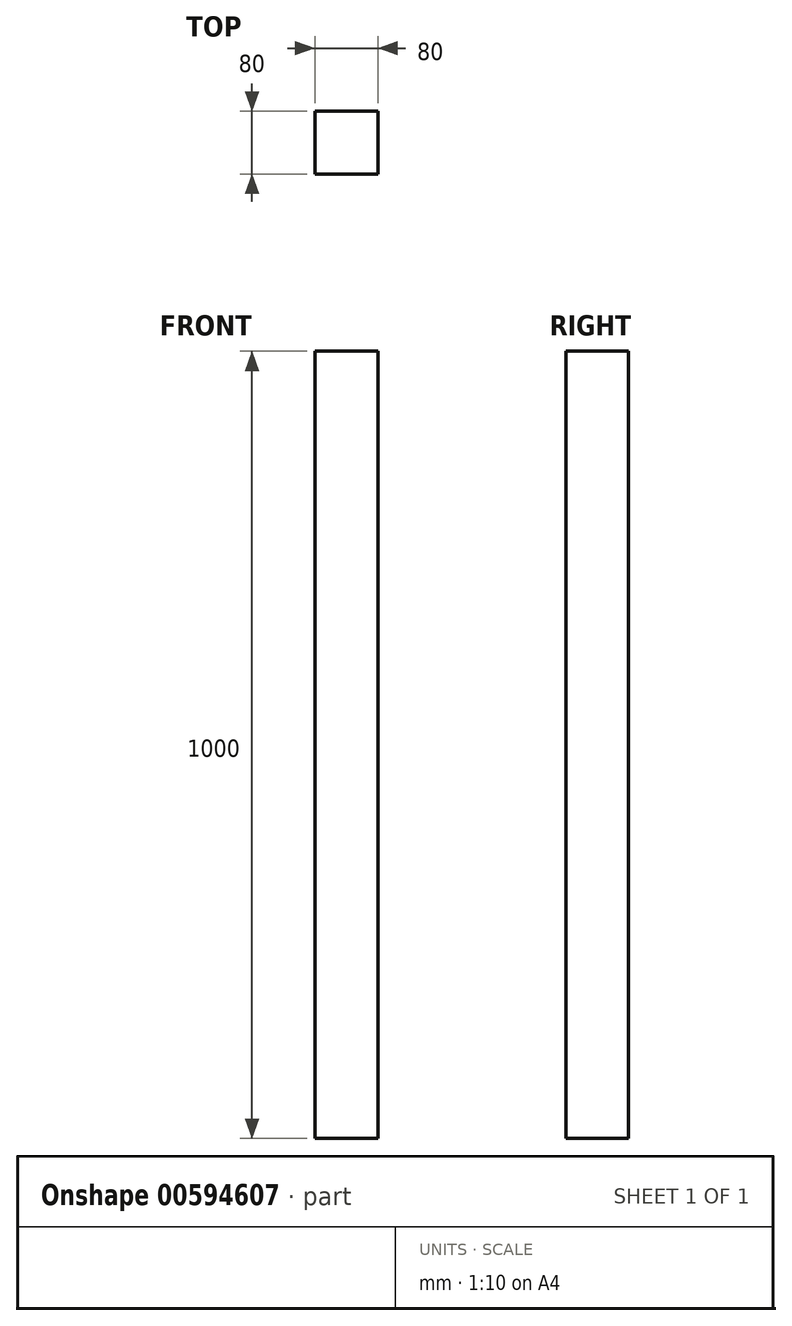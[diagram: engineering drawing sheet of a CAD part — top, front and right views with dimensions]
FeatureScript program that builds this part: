
annotation { "Feature Type Name" : "Feature", "Feature Type Description" : "" }
export const myFeature = defineFeature(function(context is Context, id is Id, definition is map)
    precondition{}
    {
        {
            var Q0;
            Q0=qCreatedBy(makeId("Top.planeOp"),FACE);
            var sketch = newSketch(context, id + "F0", { "sketchPlane" : qUnion([Q0])});
            skLineSegment(sketch, "E0.bottom", {"start": v(0, 0) * mm, "end": v(80, 0) * mm});
            skLineSegment(sketch, "E0.top", {"start": v(0, 80) * mm, "end": v(80, 80) * mm});
            skLineSegment(sketch, "E0.left", {"start": v(0, 0) * mm, "end": v(0, 80) * mm});
            skLineSegment(sketch, "E0.right", {"start": v(80, 0) * mm, "end": v(80, 80) * mm});
            skSolve(sketch);
        }
        {
            var Q0;
            Q0=qSketchRegion(id+"F0",true);
            extrude(context, id + "F1", {"entities" : qUnion([Q0]), "depth" : 1000 * mm, "offsetDistance" : 25 * mm});
        }
    });
